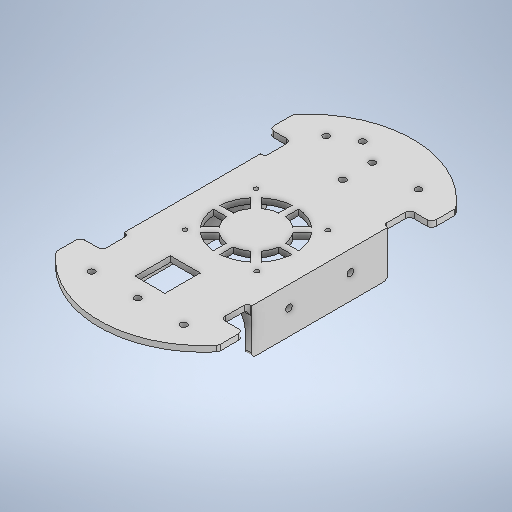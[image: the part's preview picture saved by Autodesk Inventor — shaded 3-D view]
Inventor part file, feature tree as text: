
AUTODESK INVENTOR PART (.ipt)
format: ipt  version: 2025.2 (Build 292293000, 293)  size: 739,840 bytes
history: native  units: mm
features: fillet x34, extrude x14, sketch x14
ambient origin geometry x8: Origin, YZ Plane, XZ Plane, XY Plane, X Axis, Y Axis, Z Axis, Center Point
bodies: Solid1 (feature_tree)
feature tree (62):
  extrude  "Extrusion1"  Depth=11.0mm
  fillet  "Face Fillet1"
  fillet  "Face Fillet2"
  fillet  "Face Fillet3"
  fillet  "Face Fillet4"
  fillet  "Face Fillet5"
  fillet  "Face Fillet6"
  fillet  "Face Fillet7"
  fillet  "Face Fillet8"
  fillet  "Face Fillet9"
  fillet  "Face Fillet10"
  fillet  "Face Fillet11"
  fillet  "Face Fillet12"
  extrude  "Extrusion3"  Depth=17.5mm
  sketch  "Sketch8"  dims[d23=2.0mm d24=2.0mm]
  sketch  "Sketch9"  dims[d25=2.0mm d26=2.0mm]
  extrude  "Extrusion4"  Depth=74.0mm
  sketch  "Sketch5"  dims[d16=27.0mm d17=2.6mm d18=0.0mm]
  sketch  "Sketch6"  dims[d19=2.0mm d20=2.0mm]
  sketch  "Sketch7"  dims[d21=2.0mm d22=2.0mm]
  extrude  "Extrusion11"  Depth=27.0mm
  extrude  "Extrusion12"  Depth=2.6mm TaperAngle=0.0deg
  extrude  "Extrusion13"  Depth=2.0mm
  extrude  "Extrusion14"  Depth=2.0mm
  extrude  "Extrusion15"  Depth=2.0mm
  fillet  "Face Fillet17"
  fillet  "Face Fillet18"
  fillet  "Face Fillet19"
  fillet  "Face Fillet20"
  sketch  "Sketch15"  dims[d27=2.0mm d39=0.0mm d40=40.0mm]
  extrude  "Extrusion16"  Depth=2.0mm
  extrude  "Extrusion17"  Depth=40.0mm TaperAngle=0.0deg
  sketch  "Sketch17"  dims[d48=2.0mm d49=2.0mm]
  extrude  "Extrusion18"  Depth=8.999549mm
  extrude  "Extrusion19"  Depth=2.0mm
  extrude  "Extrusion20"  Depth=12.0mm
  fillet  "Fillet1"  Radius=19.0mm
  fillet  "Fillet2"  Radius=24.0mm
  fillet  "Fillet3"  Radius=1.3mm
  fillet  "Fillet4"  Radius=1.3mm
  fillet  "Face Fillet21"
  fillet  "Face Fillet22"
  fillet  "Face Fillet23"
  fillet  "Face Fillet24"
  fillet  "Face Fillet25"
  fillet  "Face Fillet26"
  fillet  "Fillet5"  Radius=1.3mm
  fillet  "Fillet6"  Radius=1.3mm
  fillet  "Fillet7"  Radius=40.0mm
  fillet  "Fillet8"  Radius=1.5mm
  fillet  "Fillet9"  Radius=40.0mm
  fillet  "Fillet10"  Radius=1.5mm
  fillet  "Fillet11"  Radius=3.0mm
  fillet  "Fillet12"  Radius=21.0mm
  sketch  "Sketch1"  dims[d1=86.0mm d2=11.0mm]
  sketch  "Sketch3"  dims[d5=17.5mm d11=74.0mm]
  sketch  "Sketch4"  dims[d12=74.0mm d15=27.0mm]
  sketch  "Sketch16"  dims[d46=9.0mm d47=8.999549mm]
  sketch  "Sketch18"  dims[d50=2.0mm d51=12.0mm d52=19.0mm d53=24.0mm d54=1.3mm d55=1.3mm d56=1.3mm d57=1.3mm d58=40.0mm d59=0.0mm d60=1.5mm d61=40.0mm d62=0.0mm d63=1.5mm d64=3.0mm d65=21.0mm]
  sketch  "Sketch19"  dims[d66=21.0mm d67=10.0mm d68=2.9mm d69=2.9mm d70=2.9mm d71=10.9mm d72=3.0mm d73=3.0mm d74=3.0mm d75=18.0mm d76=18.0mm d77=3.0mm d78=26.9mm d79=70.0mm d80=26.9mm d81=10.5mm d82=10.5mm d83=2.0mm d84=2.0mm d85=2.0mm d86=2.0mm d87=18.0mm d88=82.0mm d89=31.0mm d90=31.0mm d91=31.0mm d92=18.0mm d118=10.0mm d119=0.0mm d120=10.0mm d121=0.0mm d122=10.0mm d123=0.0mm d124=16.0mm d125=18.0mm d126=20.6mm d127=2.0mm d128=1.0mm d129=0.0mm d130=0.0mm d131=2.0mm d132=1.0mm d133=0.0mm d134=0.0mm d135=2.0mm d136=2.0mm d137=2.0mm d138=2.0mm d139=14.0mm d140=14.0mm d141=9.3mm d142=3.0mm d143=3.0mm d144=3.0mm d145=3.0mm d146=40.0mm d147=5.0mm d148=0.0mm d149=0.0mm d150=40.0mm d151=0.0mm d152=20.0mm d153=0.0mm d154=1.5mm d155=1.5mm d156=9.0mm d157=4.0mm d158=9.0mm d159=4.0mm d160=1.5mm d161=9.0mm d162=4.0mm d163=9.0mm d164=4.0mm d165=10.0mm d166=0.0mm d167=10.0mm d168=0.0mm d169=5.0mm d170=5.0mm d171=45.0mm d172=0.0mm d173=6.67mm d174=6.67mm d175=6.67mm d176=6.67mm d177=3.0mm d178=3.0mm d179=1.4mm d180=1.4mm d181=1.4mm d182=1.4mm d183=1.4mm d184=1.4mm d185=1.4mm d186=1.4mm d187=1.4mm d188=1.4mm d189=1.4mm d190=1.4mm d112=0.5mm d113=0.872665mm d114=0.5mm d115=0.872665mm]
  sketch  "Sketch2"  dims[d3=11.0mm d4=17.5mm]
  extrude  "Extrusion2"  Depth=10.0mm
